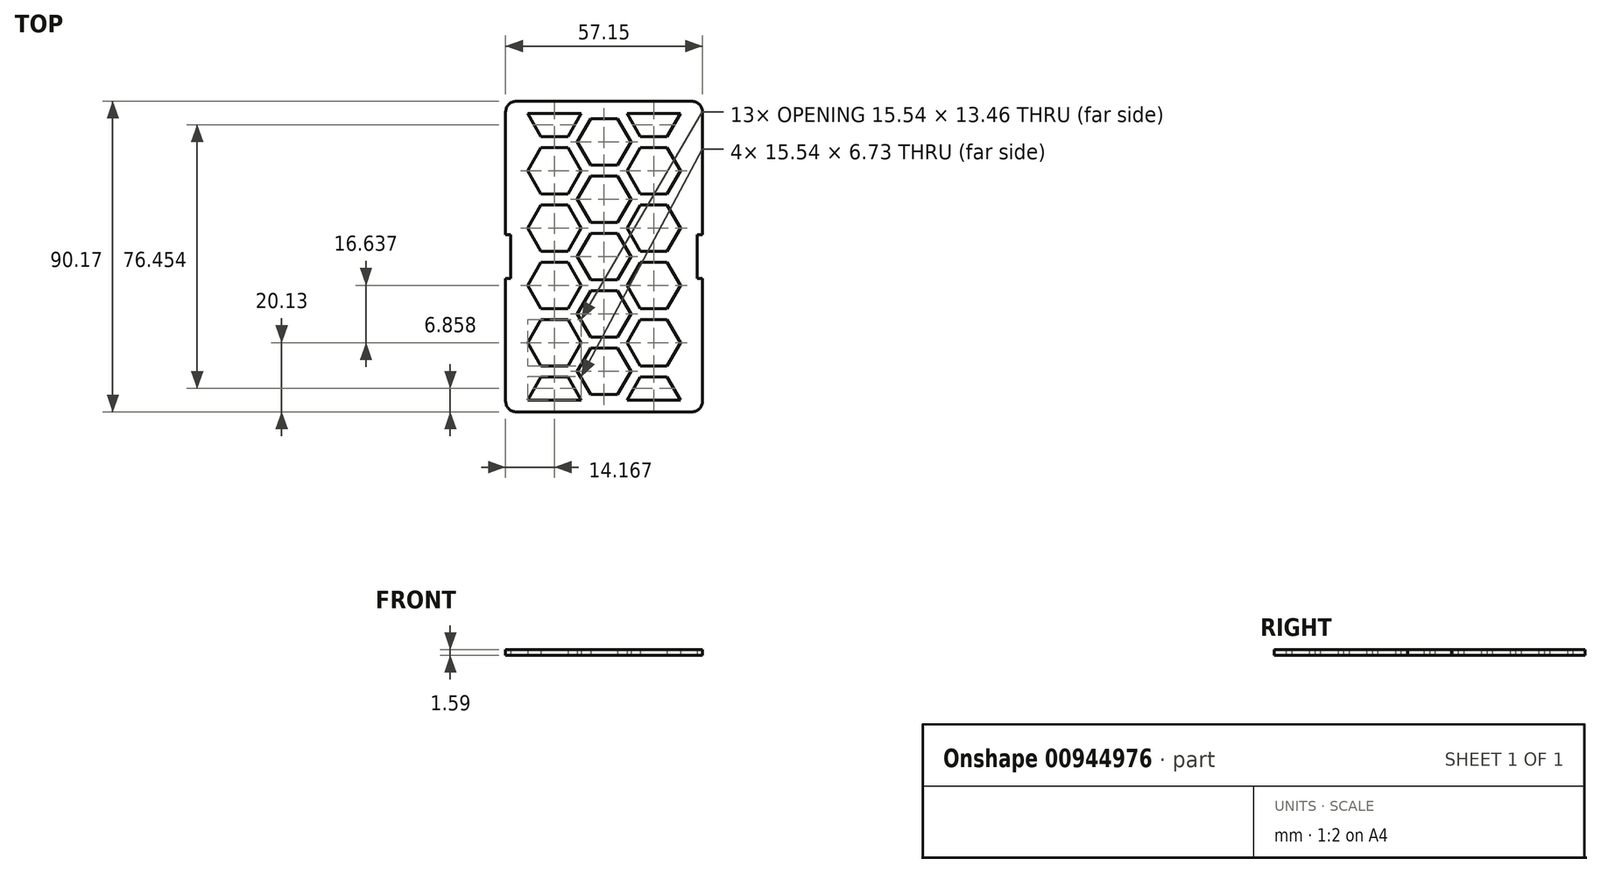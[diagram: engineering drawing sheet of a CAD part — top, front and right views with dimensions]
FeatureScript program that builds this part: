
annotation { "Feature Type Name" : "Feature", "Feature Type Description" : "" }
export const myFeature = defineFeature(function(context is Context, id is Id, definition is map)
    precondition{}
    {
        {
            var Q0;
            Q0=qCreatedBy(makeId("Top.planeOp"),FACE);
            var sketch = newSketch(context, id + "F0", { "sketchPlane" : qUnion([Q0])});
            skLineSegment(sketch, "E0.bottom", {"start": v(3.18, 0) * mm, "end": v(53.98, 0) * mm});
            skLineSegment(sketch, "E0.top", {"start": v(3.17, 90.17) * mm, "end": v(53.97, 90.17) * mm});
            skLineSegment(sketch, "E0.left", {"start": v(0, 3.18) * mm, "end": v(0, 38.74) * mm});
            skLineSegment(sketch, "E0.right", {"start": v(57.15, 3.18) * mm, "end": v(57.15, 38.74) * mm});
            skPoint(sketch, "E1.visualSharp", {"position": v(0, 90.17) * mm});
            skArc(sketch, "E1.filletArc", {"start": v(3.17, 90.17) * mm, "mid": v(0.93, 89.24) * mm, "end": v(0, 87) * mm});
            skPoint(sketch, "E2.visualSharp", {"position": v(57.15, 90.17) * mm});
            skArc(sketch, "E2.filletArc", {"start": v(57.15, 87) * mm, "mid": v(56.22, 89.24) * mm, "end": v(53.97, 90.17) * mm});
            skPoint(sketch, "E3.visualSharp", {"position": v(57.15, 0) * mm});
            skArc(sketch, "E3.filletArc", {"start": v(53.98, 0) * mm, "mid": v(56.22, 0.93) * mm, "end": v(57.15, 3.18) * mm});
            skPoint(sketch, "E4.visualSharp", {"position": v(0, 0) * mm});
            skArc(sketch, "E4.filletArc", {"start": v(0, 3.17) * mm, "mid": v(0.93, 0.93) * mm, "end": v(3.18, 0) * mm});
            skLineSegment(sketch, "E5", {"start": v(28.58, 90.17) * mm, "end": v(28.58, 0) * mm, "construction": true});
            skCircle(sketch, "E6.cCircle", {"center": v(28.58, 45.09) * mm, "radius": 6.73 * mm, "construction": true});
            skLineSegment(sketch, "E6.0", {"start": v(24.69, 51.82) * mm, "end": v(32.46, 51.82) * mm});
            skLineSegment(sketch, "E6.1", {"start": v(32.46, 51.82) * mm, "end": v(36.35, 45.08) * mm});
            skLineSegment(sketch, "E6.2", {"start": v(36.35, 45.09) * mm, "end": v(32.46, 38.35) * mm});
            skLineSegment(sketch, "E6.3", {"start": v(32.46, 38.35) * mm, "end": v(24.69, 38.35) * mm});
            skLineSegment(sketch, "E6.4", {"start": v(24.69, 38.35) * mm, "end": v(20.8, 45.09) * mm});
            skLineSegment(sketch, "E6.5", {"start": v(20.8, 45.09) * mm, "end": v(24.69, 51.82) * mm});
            skPoint(sketch, "E6.0.midPoint", {"position": v(28.58, 51.82) * mm});
            skLineSegment(sketch, "E7.0.1.0", {"start": v(32.46, 21.72) * mm, "end": v(24.69, 21.72) * mm});
            skCircle(sketch, "E7.0.1.1", {"center": v(28.58, 28.45) * mm, "radius": 6.73 * mm, "construction": true});
            skLineSegment(sketch, "E7.0.1.2", {"start": v(20.8, 28.45) * mm, "end": v(24.69, 35.18) * mm});
            skLineSegment(sketch, "E7.0.1.3", {"start": v(24.69, 35.18) * mm, "end": v(32.46, 35.18) * mm});
            skLineSegment(sketch, "E7.0.1.4", {"start": v(24.69, 21.72) * mm, "end": v(20.8, 28.45) * mm});
            skLineSegment(sketch, "E7.0.1.5", {"start": v(36.35, 28.45) * mm, "end": v(32.46, 21.72) * mm});
            skLineSegment(sketch, "E7.0.1.6", {"start": v(32.46, 35.18) * mm, "end": v(36.35, 28.45) * mm});
            skLineSegment(sketch, "E7.0.2.0", {"start": v(32.46, 5.08) * mm, "end": v(24.69, 5.08) * mm});
            skCircle(sketch, "E7.0.2.1", {"center": v(28.58, 11.81) * mm, "radius": 6.73 * mm, "construction": true});
            skLineSegment(sketch, "E7.0.2.2", {"start": v(20.8, 11.81) * mm, "end": v(24.69, 18.54) * mm});
            skLineSegment(sketch, "E7.0.2.3", {"start": v(24.69, 18.54) * mm, "end": v(32.46, 18.54) * mm});
            skLineSegment(sketch, "E7.0.2.4", {"start": v(24.69, 5.08) * mm, "end": v(20.8, 11.81) * mm});
            skLineSegment(sketch, "E7.0.2.5", {"start": v(36.35, 11.81) * mm, "end": v(32.46, 5.08) * mm});
            skLineSegment(sketch, "E7.0.2.6", {"start": v(32.46, 18.54) * mm, "end": v(36.35, 11.81) * mm});
            skLineSegment(sketch, "E7.direction1", {"start": v(24.69, 38.35) * mm, "end": v(50.09, 38.35) * mm, "construction": true});
            skLineSegment(sketch, "E7.direction2", {"start": v(24.69, 38.35) * mm, "end": v(24.69, 21.72) * mm, "construction": true});
            skLineSegment(sketch, "E8.0.1.0", {"start": v(20.8, 61.72) * mm, "end": v(24.69, 68.45) * mm});
            skLineSegment(sketch, "E8.0.1.1", {"start": v(24.69, 55) * mm, "end": v(20.8, 61.72) * mm});
            skPoint(sketch, "E8.0.1.2", {"position": v(28.58, 68.45) * mm});
            skLineSegment(sketch, "E8.0.1.3", {"start": v(24.69, 68.45) * mm, "end": v(32.46, 68.45) * mm});
            skCircle(sketch, "E8.0.1.4", {"center": v(28.58, 61.72) * mm, "radius": 6.73 * mm, "construction": true});
            skLineSegment(sketch, "E8.0.1.5", {"start": v(32.46, 68.45) * mm, "end": v(36.35, 61.72) * mm});
            skLineSegment(sketch, "E8.0.1.6", {"start": v(36.35, 61.72) * mm, "end": v(32.46, 55) * mm});
            skLineSegment(sketch, "E8.0.1.7", {"start": v(32.46, 55) * mm, "end": v(24.69, 55) * mm});
            skLineSegment(sketch, "E8.0.2.0", {"start": v(20.8, 78.36) * mm, "end": v(24.69, 85.1) * mm});
            skLineSegment(sketch, "E8.0.2.1", {"start": v(24.69, 71.63) * mm, "end": v(20.8, 78.36) * mm});
            skPoint(sketch, "E8.0.2.2", {"position": v(28.58, 85.1) * mm});
            skLineSegment(sketch, "E8.0.2.3", {"start": v(24.69, 85.1) * mm, "end": v(32.46, 85.1) * mm});
            skCircle(sketch, "E8.0.2.4", {"center": v(28.58, 78.36) * mm, "radius": 6.73 * mm, "construction": true});
            skLineSegment(sketch, "E8.0.2.5", {"start": v(32.46, 85.1) * mm, "end": v(36.35, 78.36) * mm});
            skLineSegment(sketch, "E8.0.2.6", {"start": v(36.35, 78.36) * mm, "end": v(32.46, 71.63) * mm});
            skLineSegment(sketch, "E8.0.2.7", {"start": v(32.46, 71.63) * mm, "end": v(24.69, 71.63) * mm});
            skLineSegment(sketch, "E8.direction2", {"start": v(24.69, 38.35) * mm, "end": v(24.69, 55) * mm, "construction": true});
            skCircle(sketch, "E9.cCircle", {"center": v(14.17, 70.04) * mm, "radius": 6.73 * mm, "construction": true});
            skLineSegment(sketch, "E9.0", {"start": v(10.28, 76.77) * mm, "end": v(18.05, 76.77) * mm});
            skLineSegment(sketch, "E9.1", {"start": v(18.05, 76.77) * mm, "end": v(21.94, 70.04) * mm});
            skLineSegment(sketch, "E9.2", {"start": v(21.94, 70.04) * mm, "end": v(18.05, 63.3) * mm});
            skLineSegment(sketch, "E9.3", {"start": v(18.05, 63.3) * mm, "end": v(10.28, 63.3) * mm});
            skLineSegment(sketch, "E9.4", {"start": v(10.28, 63.3) * mm, "end": v(6.4, 70.04) * mm});
            skLineSegment(sketch, "E9.5", {"start": v(6.4, 70.04) * mm, "end": v(10.28, 76.77) * mm});
            skPoint(sketch, "E9.0.midPoint", {"position": v(14.17, 76.77) * mm});
            skLineSegment(sketch, "E10.0.1.0", {"start": v(18.05, 60.13) * mm, "end": v(21.94, 53.4) * mm});
            skLineSegment(sketch, "E10.0.1.1", {"start": v(21.94, 53.4) * mm, "end": v(18.05, 46.67) * mm});
            skCircle(sketch, "E10.0.1.2", {"center": v(14.17, 53.4) * mm, "radius": 6.73 * mm, "construction": true});
            skLineSegment(sketch, "E10.0.1.3", {"start": v(6.4, 53.4) * mm, "end": v(10.28, 60.13) * mm});
            skLineSegment(sketch, "E10.0.1.4", {"start": v(10.28, 46.67) * mm, "end": v(6.4, 53.4) * mm});
            skLineSegment(sketch, "E10.0.1.5", {"start": v(10.28, 60.13) * mm, "end": v(18.05, 60.13) * mm});
            skLineSegment(sketch, "E10.0.1.6", {"start": v(18.05, 46.67) * mm, "end": v(10.28, 46.67) * mm});
            skPoint(sketch, "E10.0.1.7", {"position": v(14.17, 60.13) * mm});
            skLineSegment(sketch, "E10.0.2.0", {"start": v(18.05, 43.5) * mm, "end": v(21.94, 36.77) * mm});
            skLineSegment(sketch, "E10.0.2.1", {"start": v(21.94, 36.77) * mm, "end": v(18.05, 30.04) * mm});
            skCircle(sketch, "E10.0.2.2", {"center": v(14.17, 36.77) * mm, "radius": 6.73 * mm, "construction": true});
            skLineSegment(sketch, "E10.0.2.3", {"start": v(6.4, 36.77) * mm, "end": v(10.28, 43.5) * mm});
            skLineSegment(sketch, "E10.0.2.4", {"start": v(10.28, 30.04) * mm, "end": v(6.4, 36.77) * mm});
            skLineSegment(sketch, "E10.0.2.5", {"start": v(10.28, 43.5) * mm, "end": v(18.05, 43.5) * mm});
            skLineSegment(sketch, "E10.0.2.6", {"start": v(18.05, 30.04) * mm, "end": v(10.28, 30.04) * mm});
            skPoint(sketch, "E10.0.2.7", {"position": v(14.17, 43.5) * mm});
            skLineSegment(sketch, "E10.0.3.0", {"start": v(18.05, 26.86) * mm, "end": v(21.94, 20.13) * mm});
            skLineSegment(sketch, "E10.0.3.1", {"start": v(21.94, 20.13) * mm, "end": v(18.05, 13.4) * mm});
            skCircle(sketch, "E10.0.3.2", {"center": v(14.17, 20.13) * mm, "radius": 6.73 * mm, "construction": true});
            skLineSegment(sketch, "E10.0.3.3", {"start": v(6.4, 20.13) * mm, "end": v(10.28, 26.86) * mm});
            skLineSegment(sketch, "E10.0.3.4", {"start": v(10.28, 13.4) * mm, "end": v(6.4, 20.13) * mm});
            skLineSegment(sketch, "E10.0.3.5", {"start": v(10.28, 26.86) * mm, "end": v(18.05, 26.86) * mm});
            skLineSegment(sketch, "E10.0.3.6", {"start": v(18.05, 13.4) * mm, "end": v(10.28, 13.4) * mm});
            skPoint(sketch, "E10.0.3.7", {"position": v(14.17, 26.86) * mm});
            skLineSegment(sketch, "E10.1.0.0", {"start": v(46.86, 76.77) * mm, "end": v(50.74, 70.04) * mm});
            skLineSegment(sketch, "E10.1.0.1", {"start": v(50.74, 70.04) * mm, "end": v(46.86, 63.3) * mm});
            skCircle(sketch, "E10.1.0.2", {"center": v(42.97, 70.04) * mm, "radius": 6.73 * mm, "construction": true});
            skLineSegment(sketch, "E10.1.0.3", {"start": v(35.2, 70.04) * mm, "end": v(39.08, 76.77) * mm});
            skLineSegment(sketch, "E10.1.0.4", {"start": v(39.08, 63.3) * mm, "end": v(35.2, 70.04) * mm});
            skLineSegment(sketch, "E10.1.0.5", {"start": v(39.08, 76.77) * mm, "end": v(46.86, 76.77) * mm});
            skLineSegment(sketch, "E10.1.0.6", {"start": v(46.86, 63.3) * mm, "end": v(39.08, 63.3) * mm});
            skPoint(sketch, "E10.1.0.7", {"position": v(42.97, 76.77) * mm});
            skLineSegment(sketch, "E10.1.1.0", {"start": v(46.86, 60.13) * mm, "end": v(50.74, 53.4) * mm});
            skLineSegment(sketch, "E10.1.1.1", {"start": v(50.74, 53.4) * mm, "end": v(46.86, 46.67) * mm});
            skCircle(sketch, "E10.1.1.2", {"center": v(42.97, 53.4) * mm, "radius": 6.73 * mm, "construction": true});
            skLineSegment(sketch, "E10.1.1.3", {"start": v(35.2, 53.4) * mm, "end": v(39.08, 60.13) * mm});
            skLineSegment(sketch, "E10.1.1.4", {"start": v(39.08, 46.67) * mm, "end": v(35.2, 53.4) * mm});
            skLineSegment(sketch, "E10.1.1.5", {"start": v(39.08, 60.13) * mm, "end": v(46.86, 60.13) * mm});
            skLineSegment(sketch, "E10.1.1.6", {"start": v(46.86, 46.67) * mm, "end": v(39.08, 46.67) * mm});
            skPoint(sketch, "E10.1.1.7", {"position": v(42.97, 60.13) * mm});
            skLineSegment(sketch, "E10.1.2.0", {"start": v(46.86, 43.5) * mm, "end": v(50.74, 36.77) * mm});
            skLineSegment(sketch, "E10.1.2.1", {"start": v(50.74, 36.77) * mm, "end": v(46.86, 30.04) * mm});
            skCircle(sketch, "E10.1.2.2", {"center": v(42.97, 36.77) * mm, "radius": 6.73 * mm, "construction": true});
            skLineSegment(sketch, "E10.1.2.3", {"start": v(35.2, 36.77) * mm, "end": v(39.08, 43.5) * mm});
            skLineSegment(sketch, "E10.1.2.4", {"start": v(39.08, 30.04) * mm, "end": v(35.2, 36.77) * mm});
            skLineSegment(sketch, "E10.1.2.5", {"start": v(39.08, 43.5) * mm, "end": v(46.86, 43.5) * mm});
            skLineSegment(sketch, "E10.1.2.6", {"start": v(46.86, 30.04) * mm, "end": v(39.08, 30.04) * mm});
            skPoint(sketch, "E10.1.2.7", {"position": v(42.97, 43.5) * mm});
            skLineSegment(sketch, "E10.1.3.0", {"start": v(46.86, 26.86) * mm, "end": v(50.74, 20.13) * mm});
            skLineSegment(sketch, "E10.1.3.1", {"start": v(50.74, 20.13) * mm, "end": v(46.86, 13.4) * mm});
            skCircle(sketch, "E10.1.3.2", {"center": v(42.97, 20.13) * mm, "radius": 6.73 * mm, "construction": true});
            skLineSegment(sketch, "E10.1.3.3", {"start": v(35.2, 20.13) * mm, "end": v(39.08, 26.86) * mm});
            skLineSegment(sketch, "E10.1.3.4", {"start": v(39.08, 13.4) * mm, "end": v(35.2, 20.13) * mm});
            skLineSegment(sketch, "E10.1.3.5", {"start": v(39.08, 26.86) * mm, "end": v(46.86, 26.86) * mm});
            skLineSegment(sketch, "E10.1.3.6", {"start": v(46.86, 13.4) * mm, "end": v(39.08, 13.4) * mm});
            skPoint(sketch, "E10.1.3.7", {"position": v(42.97, 26.86) * mm});
            skLineSegment(sketch, "E10.direction1", {"start": v(18.05, 76.77) * mm, "end": v(46.86, 76.77) * mm, "construction": true});
            skLineSegment(sketch, "E10.direction2", {"start": v(18.05, 76.77) * mm, "end": v(18.05, 60.13) * mm, "construction": true});
            skLineSegment(sketch, "E11", {"start": v(0, 51.44) * mm, "end": v(1.52, 51.44) * mm});
            skLineSegment(sketch, "E12", {"start": v(1.52, 38.74) * mm, "end": v(1.52, 51.44) * mm});
            skLineSegment(sketch, "E13", {"start": v(1.52, 38.74) * mm, "end": v(0, 38.74) * mm});
            skLineSegment(sketch, "E14", {"start": v(1.52, 45.09) * mm, "end": v(28.58, 45.09) * mm, "construction": true});
            skLineSegment(sketch, "E15.trimOffspring", {"start": v(0, 51.44) * mm, "end": v(0, 87) * mm});
            skLineSegment(sketch, "E16.MirrorCS", {"start": v(55.63, 38.74) * mm, "end": v(57.15, 38.74) * mm});
            skLineSegment(sketch, "E17.MirrorCS", {"start": v(55.63, 38.74) * mm, "end": v(55.63, 51.44) * mm});
            skLineSegment(sketch, "E18.MirrorCS", {"start": v(57.15, 51.44) * mm, "end": v(55.63, 51.44) * mm});
            skLineSegment(sketch, "E19.trimOffspring", {"start": v(57.15, 51.44) * mm, "end": v(57.15, 87) * mm});
            skLineSegment(sketch, "E20.0.0.4", {"start": v(18.05, 10.22) * mm, "end": v(21.94, 3.5) * mm});
            skLineSegment(sketch, "E20.8.0.4", {"start": v(6.4, 3.5) * mm, "end": v(10.28, 10.22) * mm});
            skLineSegment(sketch, "E20.14.0.4", {"start": v(10.28, 10.22) * mm, "end": v(18.05, 10.22) * mm});
            skPoint(sketch, "E20.20.0.4", {"position": v(14.17, 10.22) * mm});
            skLineSegment(sketch, "E20.0.1.4", {"start": v(46.86, 10.22) * mm, "end": v(50.74, 3.5) * mm});
            skArc(sketch, "E20.6.1.4", {"start": v(49.7, 3.5) * mm, "mid": v(42.97, 10.22) * mm, "end": v(36.24, 3.5) * mm, "construction": true});
            skLineSegment(sketch, "E20.8.1.4", {"start": v(35.2, 3.5) * mm, "end": v(39.08, 10.22) * mm});
            skLineSegment(sketch, "E20.14.1.4", {"start": v(39.08, 10.22) * mm, "end": v(46.86, 10.22) * mm});
            skPoint(sketch, "E20.20.1.4", {"position": v(42.97, 10.22) * mm});
            skLineSegment(sketch, "E21", {"start": v(6.4, 3.5) * mm, "end": v(21.94, 3.5) * mm});
            skArc(sketch, "E22.trimOffspring", {"start": v(20.9, 3.5) * mm, "mid": v(14.17, 10.22) * mm, "end": v(7.44, 3.5) * mm, "construction": true});
            skLineSegment(sketch, "E23.trimOffspring", {"start": v(35.2, 3.5) * mm, "end": v(50.74, 3.5) * mm});
            skLineSegment(sketch, "E24.MirrorCS", {"start": v(6.4, 86.68) * mm, "end": v(21.94, 86.68) * mm});
            skLineSegment(sketch, "E25.MirrorCS", {"start": v(6.4, 86.68) * mm, "end": v(10.28, 79.95) * mm});
            skLineSegment(sketch, "E26.MirrorCS", {"start": v(10.28, 79.95) * mm, "end": v(18.05, 79.95) * mm});
            skLineSegment(sketch, "E27.MirrorCS", {"start": v(18.05, 79.95) * mm, "end": v(21.94, 86.68) * mm});
            skLineSegment(sketch, "E28.MirrorCS", {"start": v(35.2, 86.68) * mm, "end": v(50.74, 86.68) * mm});
            skLineSegment(sketch, "E29.MirrorCS", {"start": v(35.2, 86.68) * mm, "end": v(39.08, 79.95) * mm});
            skLineSegment(sketch, "E30.MirrorCS", {"start": v(39.08, 79.95) * mm, "end": v(46.86, 79.95) * mm});
            skLineSegment(sketch, "E31.MirrorCS", {"start": v(46.86, 79.95) * mm, "end": v(50.74, 86.68) * mm});
            skPoint(sketch, "E32.orphan", {"position": v(20.9, 86.68) * mm});
            skSolve(sketch);
        }
        {
            var Q0;
            Q0=makeQuery(id+"F0.imprint","IMPRINT",FACE,{"disambiguationData":[TD([[makeQuery(id+"F0.imprint","IMPRINT",EDGE,{"derivedFrom":sQuery(id+"F0.wireOp",EDGE,"E0.bottom")}),1.0]])]});
            extrude(context, id + "F1", {"entities" : qUnion([Q0]), "depth" : 1.59 * mm, "offsetDistance" : 25.4 * mm});
        }
    });
